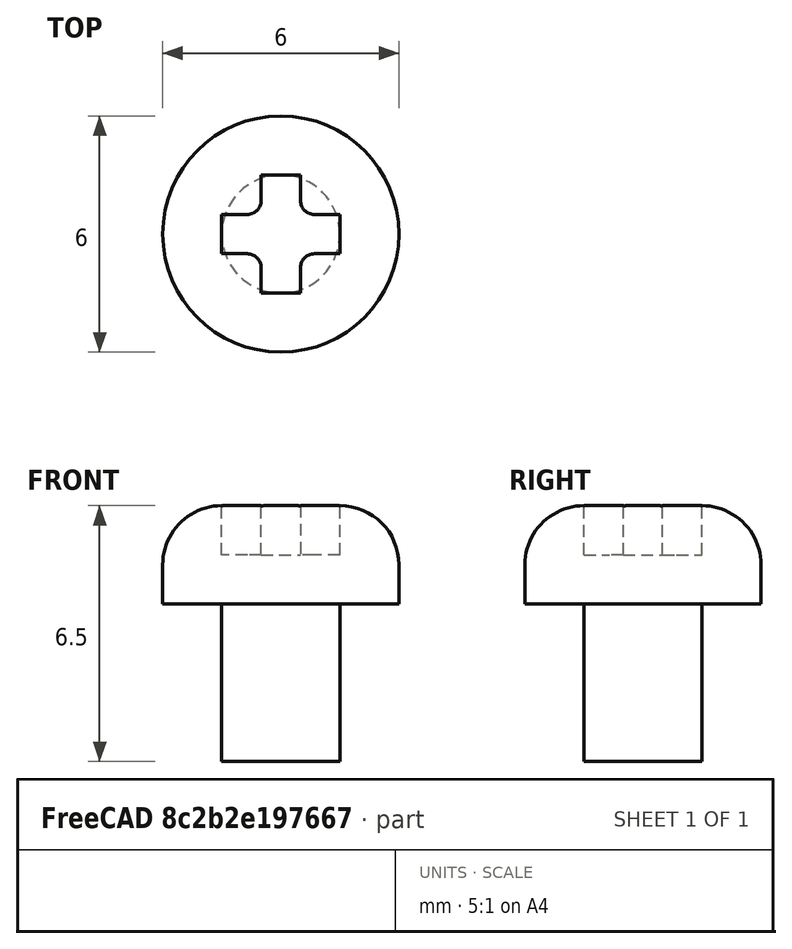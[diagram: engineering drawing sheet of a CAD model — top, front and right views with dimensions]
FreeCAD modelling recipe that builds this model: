
FCSTD DOCUMENT  (FreeCAD 0.20R)
Label: M3x4MM
License: All rights reserved
LicenseURL: http://en.wikipedia.org/wiki/All_rights_reserved
objects: Part::Cylinder×2, Part::Box×2, Part::Fillet×2, Part::Cut×2
note: 8 computed .brp shape members not serialized (recipe doc carries the construction recipe); baked Part::Feature solids carry a one-line shape summary decoded from their .brp

FEATURE [Part::Cylinder] Cylinder
  Angle = 360
  AttacherType = Attacher::AttachEngine3D
  FirstAngle = 0
  Height = 2.5
  Radius = 3
  SecondAngle = 0
FEATURE [Part::Box] Box  label="Cube"
  AttacherType = Attacher::AttachEngine3D
  Height = 1.5
  Length = 1
  Placement = pos=(-0.5,-1.5,1.25) rot=(0,0,1;0rad)
  Width = 3
FEATURE [Part::Box] Box001  label="Cube001"
  AttacherType = Attacher::AttachEngine3D
  Height = 1.5
  Length = 1
  Placement = pos=(1.5,-0.5,1.25) rot=(0,0,1;1.5708rad)
  Width = 3
FEATURE [Part::Fillet] Fillet
  Base = -> Cylinder
  Edges = 1 edges r=1.5: [Edge3]
FEATURE [Part::Cut] Cut
  Base = -> Fillet
  Refine = true
  Tool = -> Box001
FEATURE [Part::Cut] Cut001
  Base = -> Cut
  Refine = true
  Tool = -> Box
FEATURE [Part::Fillet] Fillet001
  Base = -> Cut001
  Edges = 4 edges r=0.35: [Edge29,Edge36,Edge44,Edge53]
FEATURE [Part::Cylinder] Cylinder001
  Angle = 360
  AttacherType = Attacher::AttachEngine3D
  FirstAngle = 0
  Height = 4
  Placement = pos=(0,0,-4) rot=(0,0,1;0rad)
  Radius = 1.5
  SecondAngle = 0
